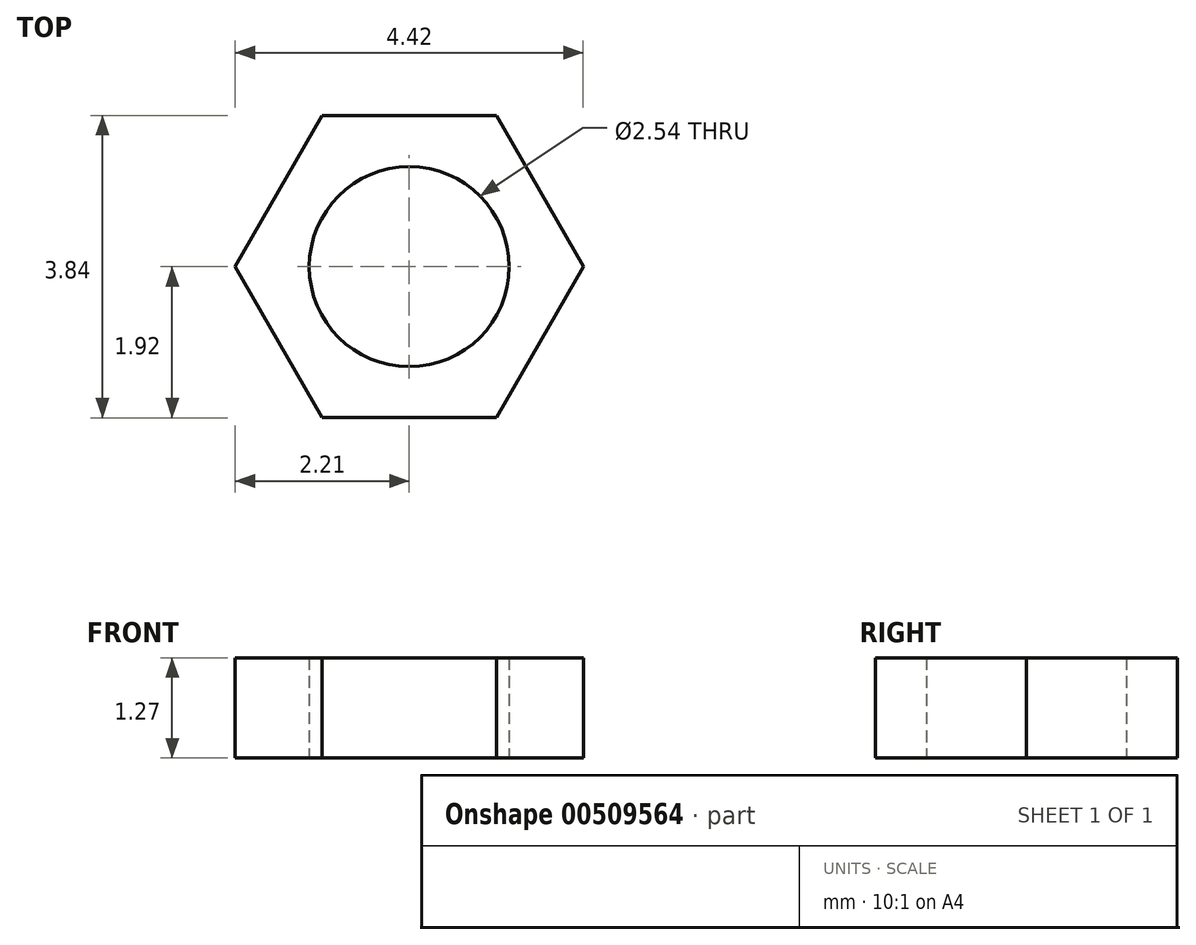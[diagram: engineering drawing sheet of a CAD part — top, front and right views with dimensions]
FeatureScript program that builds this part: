
annotation { "Feature Type Name" : "Feature", "Feature Type Description" : "" }
export const myFeature = defineFeature(function(context is Context, id is Id, definition is map)
    precondition{}
    {
        {
            var Q0;
            Q0=qCreatedBy(makeId("Top.planeOp"),FACE);
            var sketch = newSketch(context, id + "F0", { "sketchPlane" : qUnion([Q0])});
            skCircle(sketch, "E0", {"center": v(0, 0) * mm, "radius": 1.27 * mm});
            skCircle(sketch, "E1.cCircle", {"center": v(0, 0) * mm, "radius": 1.92 * mm, "construction": true});
            skLineSegment(sketch, "E1.0", {"start": v(-1.1, 1.92) * mm, "end": v(1.1, 1.92) * mm});
            skLineSegment(sketch, "E1.1", {"start": v(1.1, 1.92) * mm, "end": v(2.21, 0) * mm});
            skLineSegment(sketch, "E1.2", {"start": v(2.21, 0) * mm, "end": v(1.1, -1.92) * mm});
            skLineSegment(sketch, "E1.3", {"start": v(1.1, -1.92) * mm, "end": v(-1.1, -1.92) * mm});
            skLineSegment(sketch, "E1.4", {"start": v(-1.1, -1.92) * mm, "end": v(-2.21, 0) * mm});
            skLineSegment(sketch, "E1.5", {"start": v(-2.21, 0) * mm, "end": v(-1.1, 1.92) * mm});
            skPoint(sketch, "E1.0.midPoint", {"position": v(0, 1.92) * mm});
            skSolve(sketch);
        }
        {
            var Q0;
            Q0 = qSketchRegion(id + "F0", true);
            extrude(context, id + "F1", {"entities" : qUnion([Q0]), "depth" : 1.27 * mm});
        }
    });
